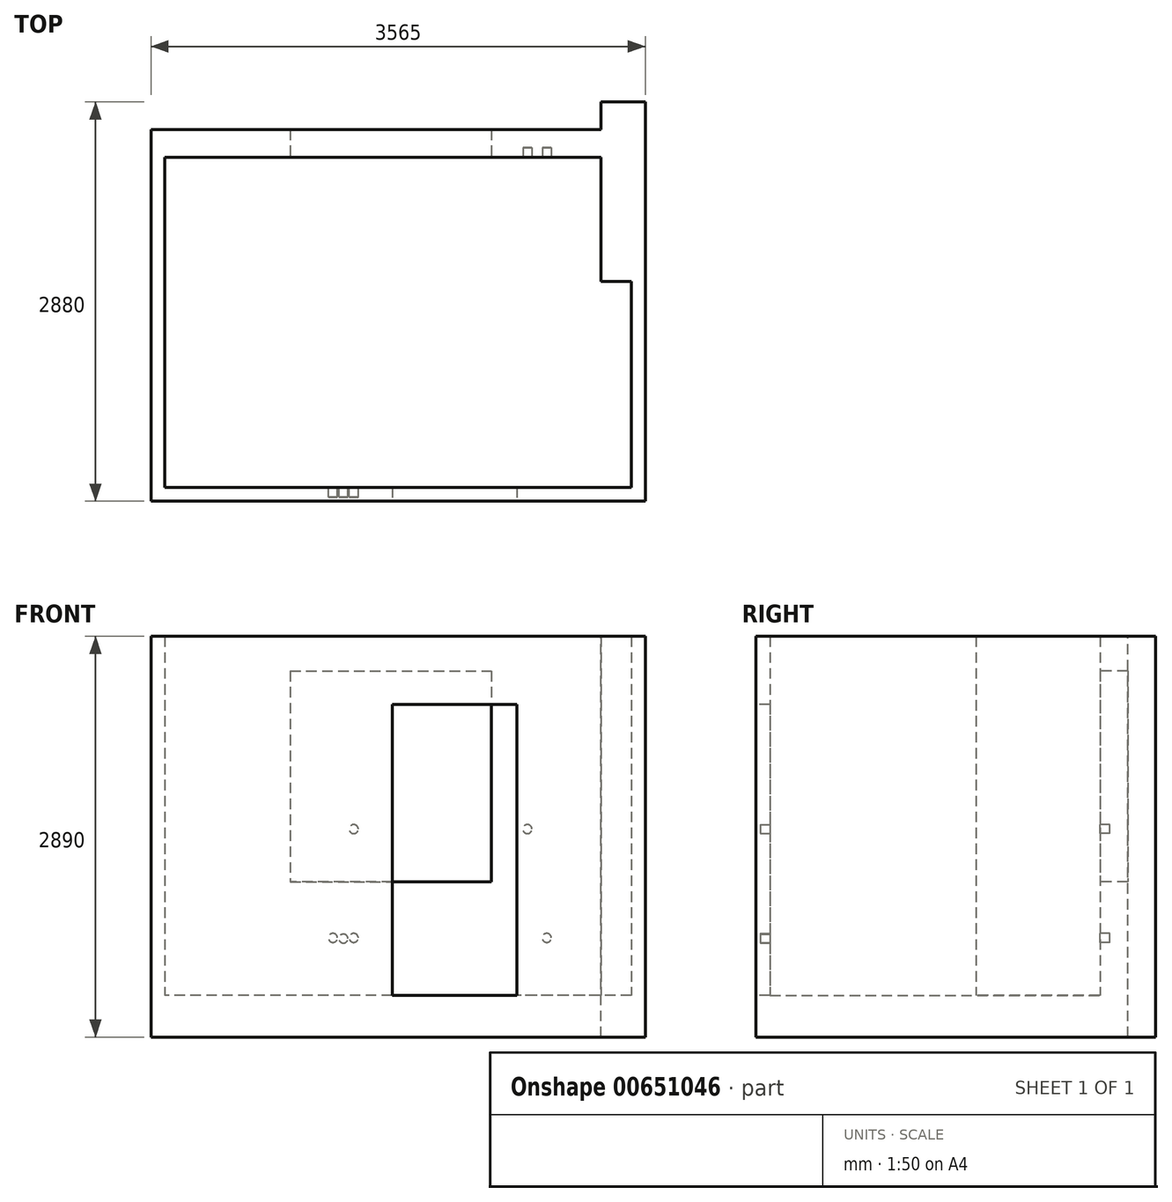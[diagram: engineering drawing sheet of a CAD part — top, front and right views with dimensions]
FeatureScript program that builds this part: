
annotation { "Feature Type Name" : "Feature", "Feature Type Description" : "" }
export const myFeature = defineFeature(function(context is Context, id is Id, definition is map)
    precondition{}
    {
        {
            var Q0;
            Q0=qCreatedBy(makeId("Top.planeOp"),FACE);
            var sketch = newSketch(context, id + "F0", { "sketchPlane" : qUnion([Q0])});
            skLineSegment(sketch, "E0.bottom", {"start": v(0, 0) * mm, "end": v(-3365, 0) * mm});
            skLineSegment(sketch, "E0.top", {"start": v(-220, 2380) * mm, "end": v(-3365, 2380) * mm});
            skLineSegment(sketch, "E0.left", {"start": v(0, 0) * mm, "end": v(0, 1485) * mm});
            skLineSegment(sketch, "E0.right", {"start": v(-3365, 0) * mm, "end": v(-3365, 2380) * mm});
            skLineSegment(sketch, "E1.bottom", {"start": v(-3465, -100) * mm, "end": v(100, -100) * mm});
            skLineSegment(sketch, "E1.top", {"start": v(-3465, 2580) * mm, "end": v(-220, 2580) * mm});
            skLineSegment(sketch, "E1.left", {"start": v(-3465, -100) * mm, "end": v(-3465, 2580) * mm});
            skLineSegment(sketch, "E1.right", {"start": v(100, -100) * mm, "end": v(100, 2580) * mm});
            skLineSegment(sketch, "E2.top", {"start": v(100, 1485) * mm, "end": v(-220, 1485) * mm});
            skLineSegment(sketch, "E2.left", {"start": v(100, 2580) * mm, "end": v(100, 1485) * mm});
            skLineSegment(sketch, "E2.right", {"start": v(-220, 2580) * mm, "end": v(-220, 1485) * mm});
            skLineSegment(sketch, "E3.bottom", {"start": v(-1725, 0) * mm, "end": v(-825, 0) * mm});
            skLineSegment(sketch, "E3.top", {"start": v(-1725, -100) * mm, "end": v(-825, -100) * mm});
            skLineSegment(sketch, "E3.left", {"start": v(-1725, 0) * mm, "end": v(-1725, -100) * mm});
            skLineSegment(sketch, "E3.right", {"start": v(-825, 0) * mm, "end": v(-825, -100) * mm});
            skLineSegment(sketch, "E4.bottom", {"start": v(-2460, 2580) * mm, "end": v(-1010, 2580) * mm});
            skLineSegment(sketch, "E4.top", {"start": v(-2460, 2380) * mm, "end": v(-1010, 2380) * mm});
            skLineSegment(sketch, "E4.left", {"start": v(-2460, 2580) * mm, "end": v(-2460, 2380) * mm});
            skLineSegment(sketch, "E4.right", {"start": v(-1010, 2580) * mm, "end": v(-1010, 2380) * mm});
            skLineSegment(sketch, "E5.top", {"start": v(-220, 2780) * mm, "end": v(100, 2780) * mm});
            skLineSegment(sketch, "E5.left", {"start": v(-220, 2580) * mm, "end": v(-220, 2780) * mm});
            skLineSegment(sketch, "E5.right", {"start": v(100, 2580) * mm, "end": v(100, 2780) * mm});
            skSolve(sketch);
        }
        {
            var Q0;
            {var subQ5=sQuery(id+"F0.wireOp",EDGE,"E0.left");Q0=makeQuery(id+"F0.imprint","IMPRINT",FACE,{"disambiguationData":[TD([[makeQuery(id+"F0.imprint","IMPRINT",EDGE,{"derivedFrom":subQ5}),1.0]])]});}
            var Q1;
            {var subQ3=sQuery(id+"F0.wireOp",EDGE,"E0.right");Q1=makeQuery(id+"F0.imprint","IMPRINT",FACE,{"disambiguationData":[TD([[makeQuery(id+"F0.imprint","IMPRINT",EDGE,{"derivedFrom":subQ3}),1.0]])]});}
            var Q2;
            {var subQ2=sQuery(id+"F0.wireOp",EDGE,"E4.left");Q2=makeQuery(id+"F0.imprint","IMPRINT",FACE,{"disambiguationData":[TD([[makeQuery(id+"F0.imprint","IMPRINT",EDGE,{"derivedFrom":subQ2}),1.0]])]});}
            var Q3;
            {var subQ0=sQuery(id+"F0.wireOp",EDGE,"E4.right");Q3=makeQuery(id+"F0.imprint","IMPRINT",FACE,{"disambiguationData":[TD([[makeQuery(id+"F0.imprint","IMPRINT",EDGE,{"derivedFrom":subQ0}),1.0]])]});}
            var Q4;
            {var subQ0=sQuery(id+"F0.wireOp",EDGE,"E3.left");Q4=makeQuery(id+"F0.imprint","IMPRINT",FACE,{"disambiguationData":[TD([[makeQuery(id+"F0.imprint","IMPRINT",EDGE,{"derivedFrom":subQ0}),1.0]])]});}
            var Q5;
            {var subQ6=sQuery(id+"F0.wireOp",EDGE,"E0.left");Q5=makeQuery(id+"F0.imprint","IMPRINT",FACE,{"disambiguationData":[TD([[makeQuery(id+"F0.imprint","IMPRINT",EDGE,{"derivedFrom":subQ6}),-1.0]])]});}
            var Q6;
            Q6=makeQuery(id+"F0.imprint","IMPRINT",FACE,{"disambiguationData":[TD([[makeQuery(id+"F0.imprint","IMPRINT",EDGE,{"derivedFrom":sQuery(id+"F0.wireOp",EDGE,"E5.top")}),-1.0]])]});
            extrude(context, id + "F1", {"entities" : qUnion([Q0, Q1, Q2, Q3, Q4, Q5, Q6]), "oppositeDirection" : true, "depth" : 300 * mm, "offsetDistance" : 25 * mm});
        }
        {
            var Q0;
            Q0=makeQuery(id+"F0.imprint","IMPRINT",FACE,{"disambiguationData":[TD([[makeQuery(id+"F0.imprint","IMPRINT",EDGE,{"derivedFrom":sQuery(id+"F0.wireOp",EDGE,"E5.top")}),-1.0]])]});
            var Q1;
            {var subQ3=sQuery(id+"F0.wireOp",EDGE,"E0.right");Q1=makeQuery(id+"F0.imprint","IMPRINT",FACE,{"disambiguationData":[TD([[makeQuery(id+"F0.imprint","IMPRINT",EDGE,{"derivedFrom":subQ3}),1.0]])]});}
            var Q2;
            {var subQ6=sQuery(id+"F0.wireOp",EDGE,"E0.left");Q2=makeQuery(id+"F0.imprint","IMPRINT",FACE,{"disambiguationData":[TD([[makeQuery(id+"F0.imprint","IMPRINT",EDGE,{"derivedFrom":subQ6}),-1.0]])]});}
            var Q3;
            {var subQ0=sQuery(id+"F0.wireOp",EDGE,"E4.right");Q3=makeQuery(id+"F0.imprint","IMPRINT",FACE,{"disambiguationData":[TD([[makeQuery(id+"F0.imprint","IMPRINT",EDGE,{"derivedFrom":subQ0}),1.0]])]});}
            extrude(context, id + "F2", {"entities" : qUnion([Q0, Q1, Q2, Q3]), "operationType" : NewBodyOperationType.ADD, "depth" : 2590 * mm, "offsetDistance" : 25 * mm});
        }
        {
            var Q0;
            {var subQ2=sQuery(id+"F0.wireOp",EDGE,"E4.left");Q0=makeQuery(id+"F0.imprint","IMPRINT",FACE,{"disambiguationData":[TD([[makeQuery(id+"F0.imprint","IMPRINT",EDGE,{"derivedFrom":subQ2}),1.0]])]});}
            extrude(context, id + "F3", {"entities" : qUnion([Q0]), "operationType" : NewBodyOperationType.ADD, "depth" : 820 * mm, "offsetDistance" : 25 * mm});
        }
        {
            var Q0;
            Q0=makeQuery(id+"F2.opExtrude","CAP_FACE",FACE,{"disambiguationData":[OSD([sQuery(id+"F0.wireOp",EDGE,"E0.bottom"),sQuery(id+"F0.wireOp",EDGE,"E0.top"),sQuery(id+"F0.wireOp",EDGE,"E0.right"),sQuery(id+"F0.wireOp",EDGE,"E1.bottom"),sQuery(id+"F0.wireOp",EDGE,"E1.top"),sQuery(id+"F0.wireOp",EDGE,"E1.left"),sQuery(id+"F0.wireOp",EDGE,"E3.left"),sQuery(id+"F0.wireOp",EDGE,"E4.left")])],"isStart":false});
            var sketch = newSketch(context, id + "F4", { "sketchPlane" : qUnion([Q0])});
            skLineSegment(sketch, "E6.0", {"start": v(-1725, 0) * mm, "end": v(-3365, 0) * mm});
            skLineSegment(sketch, "E7.0", {"start": v(-3465, -100) * mm, "end": v(-1725, -100) * mm});
            skPoint(sketch, "E8.0", {"position": v(-1725, -50) * mm});
            skLineSegment(sketch, "E9.0", {"start": v(0, 0) * mm, "end": v(-825, 0) * mm});
            skLineSegment(sketch, "E10.0", {"start": v(-825, -100) * mm, "end": v(100, -100) * mm});
            skPoint(sketch, "E11.0", {"position": v(-825, -50) * mm});
            skLineSegment(sketch, "E12.bottom", {"start": v(-1725, 0) * mm, "end": v(-825, 0) * mm});
            skLineSegment(sketch, "E12.top", {"start": v(-1725, -100) * mm, "end": v(-825, -100) * mm});
            skLineSegment(sketch, "E12.left", {"start": v(-1725, 0) * mm, "end": v(-1725, -100) * mm});
            skLineSegment(sketch, "E12.right", {"start": v(-825, 0) * mm, "end": v(-825, -100) * mm});
            skSolve(sketch);
        }
        {
            var Q0;
            Q0=qSketchRegion(id+"F4",true);
            extrude(context, id + "F5", {"entities" : qUnion([Q0]), "operationType" : NewBodyOperationType.ADD, "oppositeDirection" : true, "depth" : 490 * mm, "offsetDistance" : 25 * mm});
        }
        {
            var Q0;
            Q0=makeQuery(id+"F4.imprint","IMPRINT",FACE,{"disambiguationData":[TD([[makeQuery(id+"F4.imprint","IMPRINT",EDGE,{"derivedFrom":sQuery(id+"F4.wireOp",EDGE,"E6.0")}),1.0]])]});
            var sketch = newSketch(context, id + "F6", { "sketchPlane" : qUnion([Q0])});
            skLineSegment(sketch, "E13.0", {"start": v(-3465, 2580) * mm, "end": v(-2460, 2580) * mm});
            skLineSegment(sketch, "E14.0", {"start": v(-2460, 2380) * mm, "end": v(-3365, 2380) * mm});
            skLineSegment(sketch, "E15.0", {"start": v(-2460, 2580) * mm, "end": v(-2460, 2380) * mm});
            skLineSegment(sketch, "E16.0", {"start": v(-1010, 2580) * mm, "end": v(-220, 2580) * mm});
            skLineSegment(sketch, "E17.0", {"start": v(-220, 2380) * mm, "end": v(-1010, 2380) * mm});
            skLineSegment(sketch, "E18.0", {"start": v(-1010, 2580) * mm, "end": v(-1010, 2380) * mm});
            skLineSegment(sketch, "E19.bottom", {"start": v(-2460, 2580) * mm, "end": v(-1010, 2580) * mm});
            skLineSegment(sketch, "E19.top", {"start": v(-2460, 2380) * mm, "end": v(-1010, 2380) * mm});
            skSolve(sketch);
        }
        {
            var Q0;
            Q0=qSketchRegion(id+"F6",true);
            extrude(context, id + "F7", {"entities" : qUnion([Q0]), "operationType" : NewBodyOperationType.ADD, "oppositeDirection" : true, "depth" : 250 * mm, "offsetDistance" : 25 * mm});
        }
        {
            var Q0;
            {var subQ0=sQuery(id+"F0.wireOp",EDGE,"E0.top");Q0=makeQuery(id+"F7.boolean.opBoolean","MERGE",FACE,{"derivedFrom":[makeQuery(id+"F3.boolean.opBoolean","MERGE",FACE,{"derivedFrom":[makeQuery(id+"F2.opExtrude","SWEPT_FACE",FACE,{"disambiguationData":[OSD([subQ0]),TDD([makeQuery(id+"F0.imprint","IMPRINT",EDGE,{"disambiguationData":[TD([[makeQuery(id+"F0.imprint","INTERSECT",VERTEX,{"derivedFrom":[subQ0,sQuery(id+"F0.wireOp",EDGE,"E0.right")]}),1.0]])],"derivedFrom":subQ0})])]}),makeQuery(id+"F2.opExtrude","SWEPT_FACE",FACE,{"disambiguationData":[OSD([subQ0]),TDD([makeQuery(id+"F0.imprint","IMPRINT",EDGE,{"disambiguationData":[TD([[makeQuery(id+"F0.imprint","INTERSECT",VERTEX,{"derivedFrom":[subQ0,sQuery(id+"F0.wireOp",EDGE,"E4.right")]}),1.0]])],"derivedFrom":subQ0})])]}),makeQuery(id+"F3.opExtrude","SWEPT_FACE",FACE,{"disambiguationData":[OSD([subQ0])]})]}),makeQuery(id+"F7.opExtrude","SWEPT_FACE",FACE,{"disambiguationData":[OSD([sQuery(id+"F6.wireOp",EDGE,"E19.top")])]})]});}
            var sketch = newSketch(context, id + "F8", { "sketchPlane" : qUnion([Q0])});
            skLineSegment(sketch, "E20", {"start": v(-750, 2156.35) * mm, "end": v(-750, 274.43) * mm, "construction": true});
            skLineSegment(sketch, "E21", {"start": v(-1166.17, 1200) * mm, "end": v(300.54, 1200) * mm, "construction": true});
            skLineSegment(sketch, "E22", {"start": v(-1114.77, 415) * mm, "end": v(228.59, 415) * mm, "construction": true});
            skLineSegment(sketch, "E23.0", {"start": v(-220, 0) * mm, "end": v(-3365, 0) * mm});
            skLineSegment(sketch, "E24.0.2", {"start": v(-3365, 0) * mm, "end": v(-1725, 0) * mm});
            skLineSegment(sketch, "E24.0.4", {"start": v(-1725, 0) * mm, "end": v(-825, 0) * mm});
            skLineSegment(sketch, "E24.0.6", {"start": v(-825, 0) * mm, "end": v(0, 0) * mm});
            skLineSegment(sketch, "E24.0.8", {"start": v(0, 0) * mm, "end": v(-220, 0) * mm});
            skCircle(sketch, "E25", {"center": v(-750, 1200) * mm, "radius": 32.5 * mm});
            skLineSegment(sketch, "E26", {"start": v(-610, 552.06) * mm, "end": v(-610, 330.14) * mm, "construction": true});
            skCircle(sketch, "E27", {"center": v(-610, 415) * mm, "radius": 32.5 * mm});
            skSolve(sketch);
        }
        {
            var Q0;
            Q0=qSketchRegion(id+"F8",true);
            extrude(context, id + "F9", {"entities" : qUnion([Q0]), "operationType" : NewBodyOperationType.REMOVE, "oppositeDirection" : true, "depth" : 70 * mm, "offsetDistance" : 25 * mm});
        }
        {
            var Q0;
            {var subQ0=sQuery(id+"F0.wireOp",EDGE,"E0.bottom");Q0=makeQuery(id+"F5.boolean.opBoolean","MERGE",FACE,{"derivedFrom":[makeQuery(id+"F2.opExtrude","SWEPT_FACE",FACE,{"disambiguationData":[OSD([subQ0]),TDD([makeQuery(id+"F0.imprint","IMPRINT",EDGE,{"disambiguationData":[TD([[makeQuery(id+"F0.imprint","INTERSECT",VERTEX,{"derivedFrom":[subQ0,sQuery(id+"F0.wireOp",EDGE,"E3.left")]}),-1.0]])],"derivedFrom":subQ0})])]}),makeQuery(id+"F2.opExtrude","SWEPT_FACE",FACE,{"disambiguationData":[OSD([subQ0]),TDD([makeQuery(id+"F0.imprint","IMPRINT",EDGE,{"disambiguationData":[TD([[makeQuery(id+"F0.imprint","INTERSECT",VERTEX,{"derivedFrom":[subQ0,sQuery(id+"F0.wireOp",EDGE,"E3.right")]}),1.0]])],"derivedFrom":subQ0})])]}),makeQuery(id+"F5.opExtrude","SWEPT_FACE",FACE,{"disambiguationData":[OSD([sQuery(id+"F4.wireOp",EDGE,"E12.bottom")])]})]});}
            var sketch = newSketch(context, id + "F10", { "sketchPlane" : qUnion([Q0])});
            skLineSegment(sketch, "E28", {"start": v(2002.19, 1230.83) * mm, "end": v(2002.19, 187.55) * mm, "construction": true});
            skLineSegment(sketch, "E29", {"start": v(1898.81, 1200) * mm, "end": v(2192.96, 1200) * mm, "construction": true});
            skLineSegment(sketch, "E30", {"start": v(1879.47, 415) * mm, "end": v(2259.12, 415) * mm, "construction": true});
            skLineSegment(sketch, "E31", {"start": v(2077.19, 473.46) * mm, "end": v(2077.19, 346.65) * mm, "construction": true});
            skLineSegment(sketch, "E32", {"start": v(2152.19, 467.5) * mm, "end": v(2152.19, 345.29) * mm, "construction": true});
            skCircle(sketch, "E33", {"center": v(2002.19, 415) * mm, "radius": 32.5 * mm});
            skPoint(sketch, "E33.centerSnap0", {"position": v(2069.3, 415) * mm});
            skCircle(sketch, "E34", {"center": v(2077.19, 410.05) * mm, "radius": 32.5 * mm});
            skCircle(sketch, "E35", {"center": v(2152.19, 415) * mm, "radius": 32.5 * mm});
            skPoint(sketch, "E35.centerSnap0", {"position": v(2152.19, 406.4) * mm});
            skCircle(sketch, "E36", {"center": v(2002.19, 1200) * mm, "radius": 32.5 * mm});
            skSolve(sketch);
        }
        {
            var Q0;
            Q0=qSketchRegion(id+"F10",true);
            extrude(context, id + "F11", {"entities" : qUnion([Q0]), "operationType" : NewBodyOperationType.REMOVE, "oppositeDirection" : true, "depth" : 70 * mm, "offsetDistance" : 25 * mm});
        }
    });
